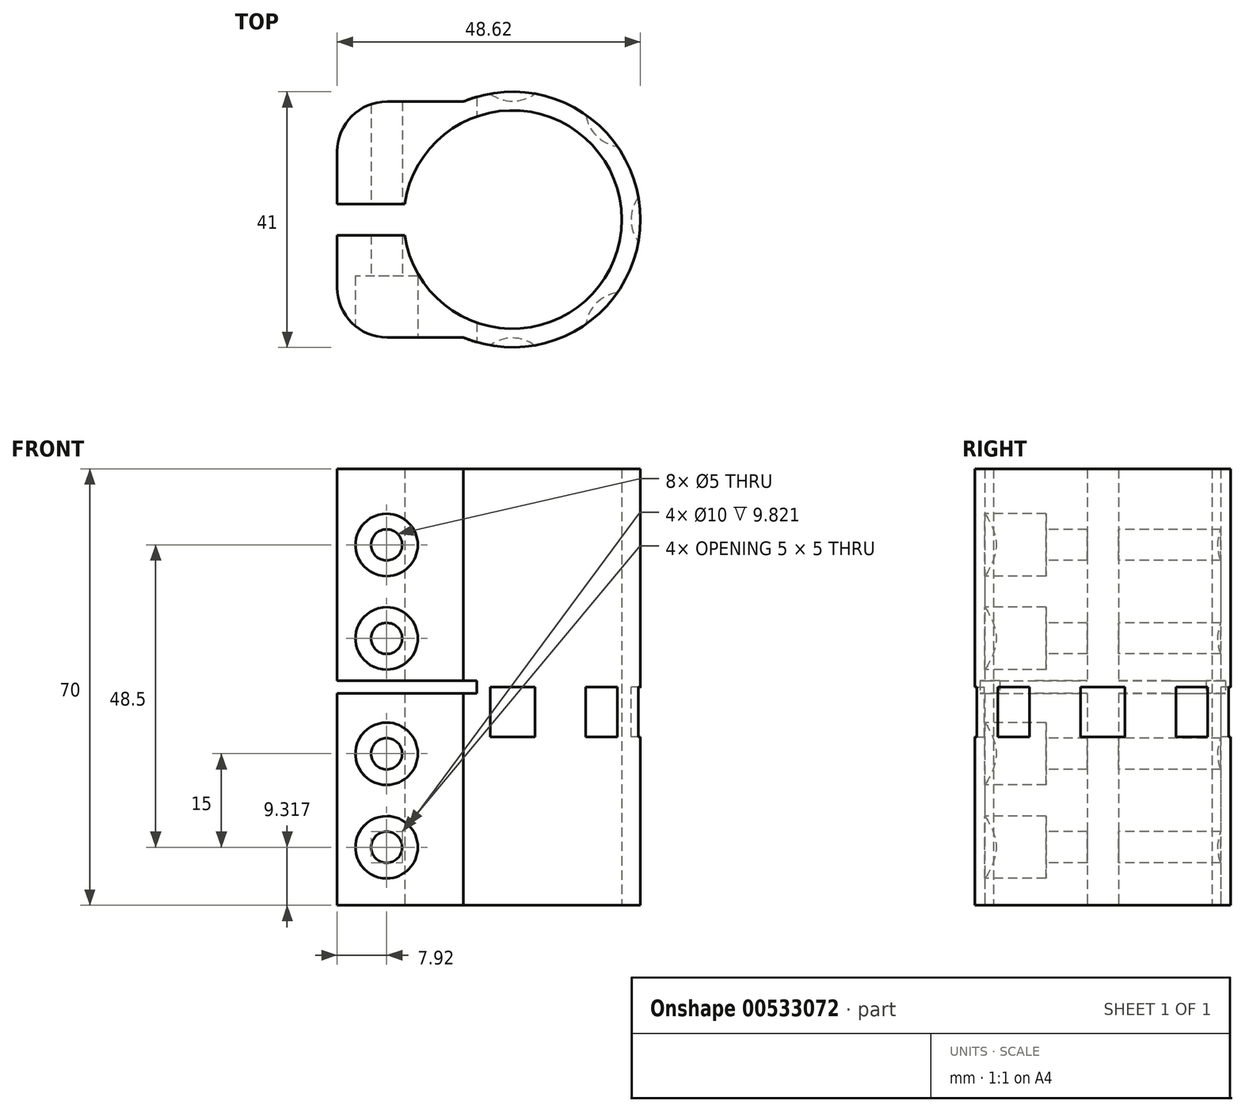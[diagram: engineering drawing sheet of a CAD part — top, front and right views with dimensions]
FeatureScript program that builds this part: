
annotation { "Feature Type Name" : "Feature", "Feature Type Description" : "" }
export const myFeature = defineFeature(function(context is Context, id is Id, definition is map)
    precondition{}
    {
        {
            var Q0;
            Q0=qCreatedBy(makeId("Top.planeOp"),FACE);
            var sketch = newSketch(context, id + "F0", { "sketchPlane" : qUnion([Q0])});
            skArc(sketch, "E0", {"start": v(-17.32, -2.5) * mm, "mid": v(17.5, 0) * mm, "end": v(-17.32, 2.5) * mm});
            skArc(sketch, "E1", {"start": v(-7.92, -18.9) * mm, "mid": v(20.5, 0) * mm, "end": v(-7.92, 18.9) * mm});
            skLineSegment(sketch, "E2", {"start": v(-7.92, 18.9) * mm, "end": v(-20.12, 18.9) * mm});
            skLineSegment(sketch, "E3", {"start": v(-28.12, 10.9) * mm, "end": v(-28.12, 2.5) * mm});
            skLineSegment(sketch, "E4", {"start": v(-28.12, 2.5) * mm, "end": v(-17.32, 2.5) * mm});
            skPoint(sketch, "E5.visualSharp", {"position": v(-28.12, 18.9) * mm});
            skArc(sketch, "E5.filletArc", {"start": v(-20.12, 18.9) * mm, "mid": v(-25.78, 16.57) * mm, "end": v(-28.12, 10.9) * mm});
            skLineSegment(sketch, "E6", {"start": v(0, 0) * mm, "end": v(33.48, 0) * mm, "construction": true});
            skLineSegment(sketch, "E7.MirrorCS", {"start": v(-7.92, -18.9) * mm, "end": v(-20.12, -18.9) * mm});
            skArc(sketch, "E8.MirrorCS", {"start": v(-20.12, -18.9) * mm, "mid": v(-25.78, -16.57) * mm, "end": v(-28.12, -10.9) * mm});
            skLineSegment(sketch, "E9.MirrorCS", {"start": v(-28.12, -10.9) * mm, "end": v(-28.12, -2.5) * mm});
            skLineSegment(sketch, "E10.MirrorCS", {"start": v(-28.12, -2.5) * mm, "end": v(-17.32, -2.5) * mm});
            skSolve(sketch);
        }
        {
            var Q0;
            Q0 = qSketchRegion(id + "F0", true);
            extrude(context, id + "F1", {"entities" : qUnion([Q0]), "depth" : 70 * mm, "offsetDistance" : 25 * mm, "symmetric" : true});
        }
        {
            var Q0;
            Q0=makeQuery(id+"F1.opExtrude","SWEPT_FACE",FACE,{"disambiguationData":[OSD([sQuery(id+"F0.wireOp",EDGE,"E7.MirrorCS")])]});
            var sketch = newSketch(context, id + "F2", { "sketchPlane" : qUnion([Q0])});
            skPoint(sketch, "E11", {"position": v(-20.2, -25.68) * mm});
            skPoint(sketch, "E12", {"position": v(-20.2, -10.68) * mm});
            skPoint(sketch, "E13", {"position": v(-20.2, 22.82) * mm});
            skPoint(sketch, "E14", {"position": v(-20.2, 7.82) * mm});
            skSolve(sketch);
        }
        {
            var Q0;
            Q0=sQuery(id+"F2.wireOp",VERTEX,"E11");
            var Q1;
            Q1=sQuery(id+"F2.wireOp",VERTEX,"E12");
            var Q2;
            Q2=sQuery(id+"F2.wireOp",VERTEX,"E14");
            var Q3;
            Q3=sQuery(id+"F2.wireOp",VERTEX,"E13");
            var Q4;
            Q4=makeQuery(id+"F1.opExtrude","SWEPT_BODY",BODY,{"disambiguationData":[OSD([sQuery(id+"F0.wireOp",EDGE,"E0"),sQuery(id+"F0.wireOp",EDGE,"E1"),sQuery(id+"F0.wireOp",EDGE,"E2"),sQuery(id+"F0.wireOp",EDGE,"E3"),sQuery(id+"F0.wireOp",EDGE,"E4"),sQuery(id+"F0.wireOp",EDGE,"E5.filletArc"),sQuery(id+"F0.wireOp",EDGE,"E7.MirrorCS"),sQuery(id+"F0.wireOp",EDGE,"E8.MirrorCS"),sQuery(id+"F0.wireOp",EDGE,"E9.MirrorCS"),sQuery(id+"F0.wireOp",EDGE,"E10.MirrorCS")])]});
            hole(context, id + "F3", {"style" : HoleStyle.C_BORE, "endStyle" : HoleEndStyle.THROUGH, "holeDiameter" : 5 * mm, "cBoreDiameter" : 10 * mm, "cBoreDepth" : 8 * mm, "majorDiameter" : 5 * mm, "isTappedThrough" : true, "tappedDepth" : 12 * mm, "tapClearance" : 3, "locations" : qUnion([Q0, Q1, Q2, Q3]), "scope" : qUnion([Q4])});
        }
        {
            var Q0;
            Q0=qCreatedBy(makeId("Front.planeOp"),FACE);
            var sketch = newSketch(context, id + "F4", { "sketchPlane" : qUnion([Q0])});
            skLineSegment(sketch, "E15.bottom", {"start": v(-28.12, 1) * mm, "end": v(-5.72, 1) * mm});
            skLineSegment(sketch, "E15.top", {"start": v(-28.12, -1) * mm, "end": v(-5.72, -1) * mm});
            skLineSegment(sketch, "E15.left", {"start": v(-28.12, 1) * mm, "end": v(-28.12, -1) * mm});
            skLineSegment(sketch, "E15.right", {"start": v(-5.72, 1) * mm, "end": v(-5.72, -1) * mm});
            skSolve(sketch);
        }
        {
            var Q0;
            Q0 = qSketchRegion(id + "F4", true);
            extrude(context, id + "F5", {"entities" : qUnion([Q0]), "operationType" : NewBodyOperationType.REMOVE, "oppositeDirection" : true, "depth" : 55 * mm, "offsetDistance" : 25 * mm, "symmetric" : true});
        }
        {
            var Q0;
            Q0=qCreatedBy(makeId("Top.planeOp"),FACE);
            var sketch = newSketch(context, id + "F6", { "sketchPlane" : qUnion([Q0])});
            skCircle(sketch, "E16", {"center": v(0, -25) * mm, "radius": 6 * mm});
            skCircle(sketch, "E17.1.0", {"center": v(17.68, -17.68) * mm, "radius": 6 * mm});
            skCircle(sketch, "E17.2.0", {"center": v(25, 0) * mm, "radius": 6 * mm});
            skCircle(sketch, "E17.3.0", {"center": v(17.68, 17.68) * mm, "radius": 6 * mm});
            skCircle(sketch, "E17.4.0", {"center": v(0, 25) * mm, "radius": 6 * mm});
            skPoint(sketch, "E17.center", {"position": v(0, 0) * mm});
            skLineSegment(sketch, "E17.anchor1", {"start": v(0, 0) * mm, "end": v(0, -25) * mm, "construction": true});
            skLineSegment(sketch, "E17.anchor2", {"start": v(0, 0) * mm, "end": v(0, 25) * mm, "construction": true});
            skSolve(sketch);
        }
        {
            var Q0;
            Q0 = qSketchRegion(id + "F6", true);
            extrude(context, id + "F7", {"entities" : qUnion([Q0]), "operationType" : NewBodyOperationType.REMOVE, "oppositeDirection" : true, "depth" : 8 * mm, "offsetDistance" : 25 * mm});
        }
    });
